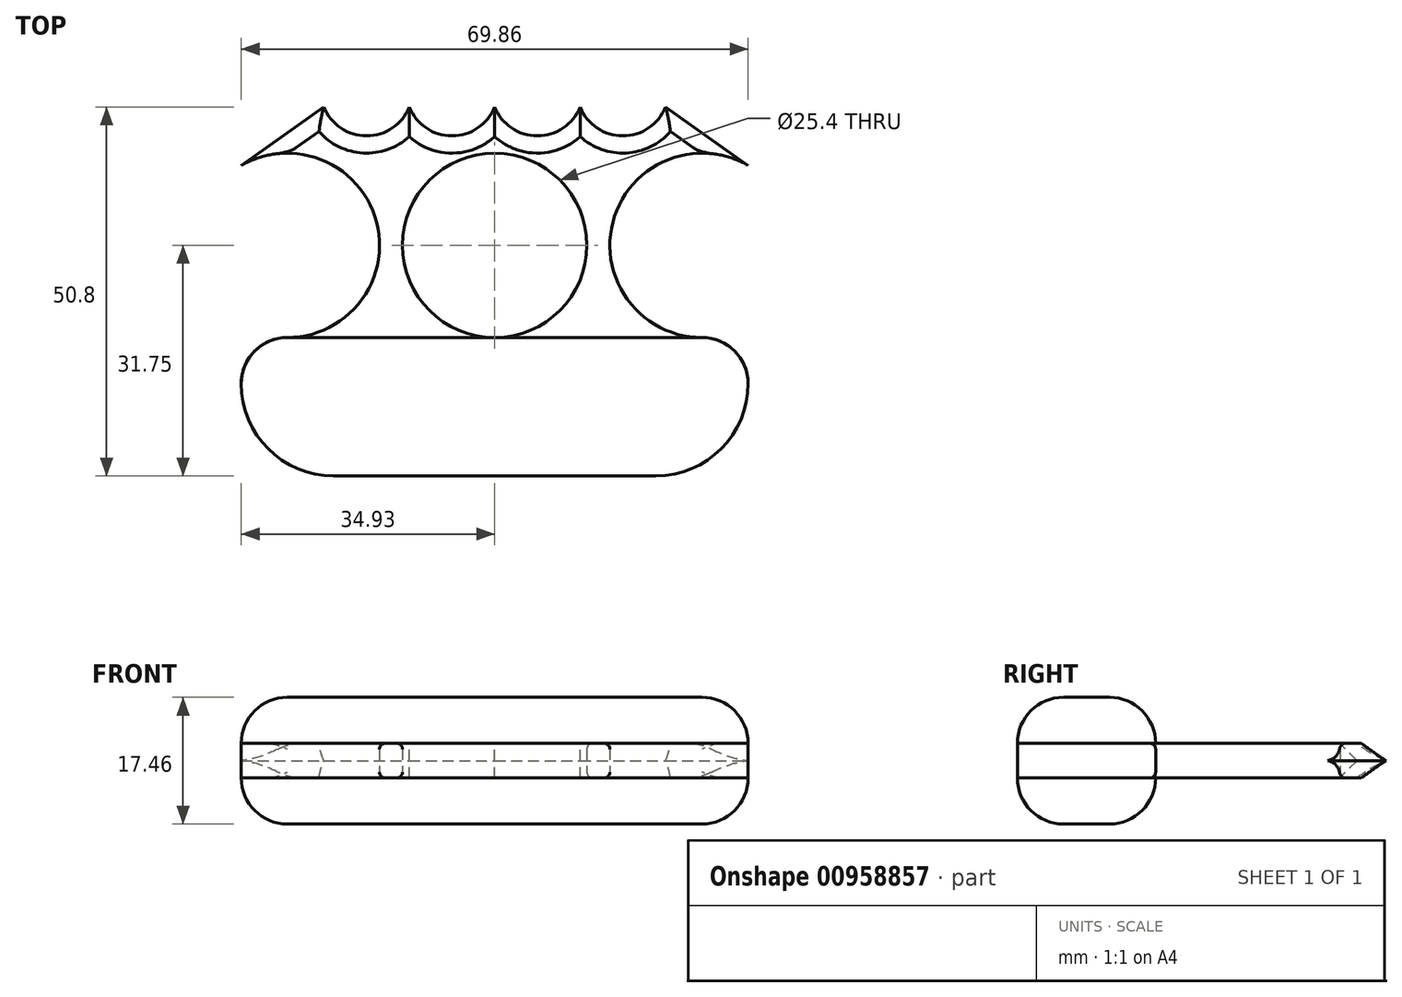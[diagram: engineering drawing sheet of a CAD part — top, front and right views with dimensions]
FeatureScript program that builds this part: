
annotation { "Feature Type Name" : "Feature", "Feature Type Description" : "" }
export const myFeature = defineFeature(function(context is Context, id is Id, definition is map)
    precondition{}
    {
        {
            var Q0;
            Q0=qCreatedBy(makeId("Top.planeOp"),FACE);
            var sketch = newSketch(context, id + "F0", { "sketchPlane" : qUnion([Q0])});
            skLineSegment(sketch, "E0.bottom", {"start": v(34.92, -25.4) * mm, "end": v(-34.92, -25.4) * mm});
            skLineSegment(sketch, "E0.top", {"start": v(34.92, 25.4) * mm, "end": v(-34.93, 25.4) * mm, "construction": true});
            skLineSegment(sketch, "E0.left", {"start": v(34.93, -25.4) * mm, "end": v(34.93, 25.4) * mm, "construction": true});
            skLineSegment(sketch, "E0.right", {"start": v(-34.92, -25.4) * mm, "end": v(-34.92, 25.4) * mm, "construction": true});
            skPoint(sketch, "E0.middle", {"position": v(0, 0) * mm});
            skCircle(sketch, "E1", {"center": v(0, 6.35) * mm, "radius": 12.7 * mm});
            skLineSegment(sketch, "E2", {"start": v(0, -6.35) * mm, "end": v(-34.92, -6.35) * mm, "construction": true});
            skLineSegment(sketch, "E3", {"start": v(0, -6.35) * mm, "end": v(34.93, -6.35) * mm, "construction": true});
            skArc(sketch, "E4", {"start": v(28.57, -6.35) * mm, "mid": v(16.3, 9.64) * mm, "end": v(34.92, 17.35) * mm});
            skArc(sketch, "E5", {"start": v(-28.58, -6.35) * mm, "mid": v(-16.3, 9.64) * mm, "end": v(-34.93, 17.35) * mm});
            skArc(sketch, "E6", {"start": v(28.57, -6.35) * mm, "mid": v(33.07, -8.2) * mm, "end": v(34.93, -12.7) * mm});
            skArc(sketch, "E7", {"start": v(-28.58, -6.35) * mm, "mid": v(-33.07, -8.2) * mm, "end": v(-34.93, -12.7) * mm});
            skArc(sketch, "E8", {"start": v(-34.93, -12.7) * mm, "mid": v(-31.2, -21.68) * mm, "end": v(-22.23, -25.4) * mm});
            skArc(sketch, "E9", {"start": v(34.93, -12.7) * mm, "mid": v(31.2, -21.68) * mm, "end": v(22.22, -25.4) * mm});
            skArc(sketch, "E10", {"start": v(-11.77, 25.4) * mm, "mid": v(-5.89, 21.43) * mm, "end": v(0, 25.4) * mm});
            skArc(sketch, "E11", {"start": v(-23.55, 25.4) * mm, "mid": v(-17.66, 21.43) * mm, "end": v(-11.77, 25.4) * mm});
            skLineSegment(sketch, "E12", {"start": v(-23.55, 25.4) * mm, "end": v(-34.93, 17.35) * mm});
            skLineSegment(sketch, "E13", {"start": v(0, 25.4) * mm, "end": v(0, -25.4) * mm, "construction": true});
            skArc(sketch, "E14.MirrorCS", {"start": v(11.77, 25.4) * mm, "mid": v(5.89, 21.43) * mm, "end": v(0, 25.4) * mm});
            skArc(sketch, "E15.MirrorCS", {"start": v(23.55, 25.4) * mm, "mid": v(17.66, 21.43) * mm, "end": v(11.77, 25.4) * mm});
            skLineSegment(sketch, "E16.MirrorCS", {"start": v(23.55, 25.4) * mm, "end": v(34.93, 17.35) * mm});
            skSolve(sketch);
        }
        {
            var Q0;
            Q0=makeQuery(id+"F0.imprint","IMPRINT",FACE,{"disambiguationData":[TD([[makeQuery(id+"F0.imprint","IMPRINT",EDGE,{"derivedFrom":sQuery(id+"F0.wireOp",EDGE,"E1")}),-1.0]])]});
            extrude(context, id + "F1", {"entities" : qUnion([Q0]), "depth" : 4.76 * mm, "offsetDistance" : 25.4 * mm});
        }
        {
            var Q0;
            Q0=makeQuery(id+"F1.opExtrude","CAP_EDGE",EDGE,{"disambiguationData":[OSD([sQuery(id+"F0.wireOp",EDGE,"E15.MirrorCS")])],"isStart":false});
            var Q1;
            Q1=makeQuery(id+"F1.opExtrude","CAP_EDGE",EDGE,{"disambiguationData":[OSD([sQuery(id+"F0.wireOp",EDGE,"E14.MirrorCS")])],"isStart":false});
            var Q2;
            Q2=makeQuery(id+"F1.opExtrude","CAP_EDGE",EDGE,{"disambiguationData":[OSD([sQuery(id+"F0.wireOp",EDGE,"E10")])],"isStart":false});
            var Q3;
            Q3=makeQuery(id+"F1.opExtrude","CAP_EDGE",EDGE,{"disambiguationData":[OSD([sQuery(id+"F0.wireOp",EDGE,"E11")])],"isStart":false});
            var Q4;
            Q4=makeQuery(id+"F1.opExtrude","CAP_EDGE",EDGE,{"disambiguationData":[OSD([sQuery(id+"F0.wireOp",EDGE,"E15.MirrorCS")])],"isStart":true});
            var Q5;
            Q5=makeQuery(id+"F1.opExtrude","CAP_EDGE",EDGE,{"disambiguationData":[OSD([sQuery(id+"F0.wireOp",EDGE,"E14.MirrorCS")])],"isStart":true});
            var Q6;
            Q6=makeQuery(id+"F1.opExtrude","CAP_EDGE",EDGE,{"disambiguationData":[OSD([sQuery(id+"F0.wireOp",EDGE,"E10")])],"isStart":true});
            var Q7;
            Q7=makeQuery(id+"F1.opExtrude","CAP_EDGE",EDGE,{"disambiguationData":[OSD([sQuery(id+"F0.wireOp",EDGE,"E11")])],"isStart":true});
            var Q8;
            Q8=makeQuery(id+"F1.opExtrude","CAP_EDGE",EDGE,{"disambiguationData":[OSD([sQuery(id+"F0.wireOp",EDGE,"E16.MirrorCS")])],"isStart":false});
            var Q9;
            Q9=makeQuery(id+"F1.opExtrude","CAP_EDGE",EDGE,{"disambiguationData":[OSD([sQuery(id+"F0.wireOp",EDGE,"E16.MirrorCS")])],"isStart":true});
            var Q10;
            Q10=makeQuery(id+"F1.opExtrude","CAP_EDGE",EDGE,{"disambiguationData":[OSD([sQuery(id+"F0.wireOp",EDGE,"E12")])],"isStart":false});
            var Q11;
            Q11=makeQuery(id+"F1.opExtrude","CAP_EDGE",EDGE,{"disambiguationData":[OSD([sQuery(id+"F0.wireOp",EDGE,"E12")])],"isStart":true});
            chamfer(context, id + "F2", {"entities" : qUnion([Q0, Q1, Q2, Q3, Q4, Q5, Q6, Q7, Q8, Q9, Q10, Q11]), "width" : 2.38 * mm, "tangentPropagation" : true});
        }
        {
            var Q0;
            Q0=makeQuery(id+"F1.opExtrude","CAP_FACE",FACE,{"disambiguationData":[OSD([sQuery(id+"F0.wireOp",EDGE,"E0.bottom"),sQuery(id+"F0.wireOp",EDGE,"E1"),sQuery(id+"F0.wireOp",EDGE,"E4"),sQuery(id+"F0.wireOp",EDGE,"E5"),sQuery(id+"F0.wireOp",EDGE,"E6"),sQuery(id+"F0.wireOp",EDGE,"E7"),sQuery(id+"F0.wireOp",EDGE,"E8"),sQuery(id+"F0.wireOp",EDGE,"E9"),sQuery(id+"F0.wireOp",EDGE,"E10"),sQuery(id+"F0.wireOp",EDGE,"E11"),sQuery(id+"F0.wireOp",EDGE,"E12"),sQuery(id+"F0.wireOp",EDGE,"E14.MirrorCS"),sQuery(id+"F0.wireOp",EDGE,"E15.MirrorCS"),sQuery(id+"F0.wireOp",EDGE,"E16.MirrorCS")])],"isStart":false});
            var sketch = newSketch(context, id + "F3", { "sketchPlane" : qUnion([Q0])});
            skLineSegment(sketch, "E17", {"start": v(-28.58, -6.35) * mm, "end": v(28.57, -6.35) * mm});
            skSolve(sketch);
        }
        {
            var Q0;
            Q0=makeQuery(id+"F3.imprint","IMPRINT",FACE,{"disambiguationData":[TD([[makeQuery(id+"F3.imprint","IMPRINT",EDGE,{"derivedFrom":makeQuery(id+"F1.opExtrude","CAP_EDGE",EDGE,{"disambiguationData":[OSD([sQuery(id+"F0.wireOp",EDGE,"E0.bottom")])],"isStart":false})}),-1.0]])]});
            extrude(context, id + "F4", {"entities" : qUnion([Q0]), "depth" : 6.35 * mm, "offsetDistance" : 25.4 * mm});
        }
        {
            var Q0;
            Q0=makeQuery(id+"F1.opExtrude","CAP_FACE",FACE,{"disambiguationData":[OSD([sQuery(id+"F0.wireOp",EDGE,"E0.bottom"),sQuery(id+"F0.wireOp",EDGE,"E1"),sQuery(id+"F0.wireOp",EDGE,"E4"),sQuery(id+"F0.wireOp",EDGE,"E5"),sQuery(id+"F0.wireOp",EDGE,"E6"),sQuery(id+"F0.wireOp",EDGE,"E7"),sQuery(id+"F0.wireOp",EDGE,"E8"),sQuery(id+"F0.wireOp",EDGE,"E9"),sQuery(id+"F0.wireOp",EDGE,"E10"),sQuery(id+"F0.wireOp",EDGE,"E11"),sQuery(id+"F0.wireOp",EDGE,"E12"),sQuery(id+"F0.wireOp",EDGE,"E14.MirrorCS"),sQuery(id+"F0.wireOp",EDGE,"E15.MirrorCS"),sQuery(id+"F0.wireOp",EDGE,"E16.MirrorCS")])],"isStart":true});
            var sketch = newSketch(context, id + "F5", { "sketchPlane" : qUnion([Q0])});
            skLineSegment(sketch, "E18", {"start": v(-28.58, 6.35) * mm, "end": v(28.57, 6.35) * mm});
            skSolve(sketch);
        }
        {
            var Q0;
            Q0=makeQuery(id+"F5.imprint","IMPRINT",FACE,{"disambiguationData":[TD([[makeQuery(id+"F5.imprint","IMPRINT",EDGE,{"derivedFrom":makeQuery(id+"F1.opExtrude","CAP_EDGE",EDGE,{"disambiguationData":[OSD([sQuery(id+"F0.wireOp",EDGE,"E0.bottom")])],"isStart":true})}),1.0]])]});
            extrude(context, id + "F6", {"entities" : qUnion([Q0]), "depth" : 6.35 * mm, "offsetDistance" : 25.4 * mm});
        }
        {
            var Q0;
            Q0=makeQuery(id+"F4.opExtrude","CAP_FACE",FACE,{"disambiguationData":[OSD([sQuery(id+"F0.wireOp",EDGE,"E0.bottom"),sQuery(id+"F0.wireOp",EDGE,"E6"),sQuery(id+"F0.wireOp",EDGE,"E7"),sQuery(id+"F0.wireOp",EDGE,"E8"),sQuery(id+"F0.wireOp",EDGE,"E9"),sQuery(id+"F3.wireOp",EDGE,"E17")])],"isStart":false});
            var Q1;
            Q1=makeQuery(id+"F6.opExtrude","CAP_FACE",FACE,{"disambiguationData":[OSD([sQuery(id+"F0.wireOp",EDGE,"E0.bottom"),sQuery(id+"F0.wireOp",EDGE,"E6"),sQuery(id+"F0.wireOp",EDGE,"E7"),sQuery(id+"F0.wireOp",EDGE,"E8"),sQuery(id+"F0.wireOp",EDGE,"E9"),sQuery(id+"F5.wireOp",EDGE,"E18")])],"isStart":false});
            fillet(context, id + "F7", {"entities" : qUnion([Q0, Q1]), "radius" : 6.35 * mm, "tangentPropagation" : true, "allowEdgeOverflow" : false});
        }
        {
            var Q0;
            Q0=makeQuery(id+"F1.opExtrude","CAP_EDGE",EDGE,{"disambiguationData":[OSD([sQuery(id+"F0.wireOp",EDGE,"E4")])],"isStart":true});
            var Q1;
            Q1=makeQuery(id+"F1.opExtrude","CAP_EDGE",EDGE,{"disambiguationData":[OSD([sQuery(id+"F0.wireOp",EDGE,"E1")])],"isStart":true});
            var Q2;
            Q2=makeQuery(id+"F1.opExtrude","CAP_EDGE",EDGE,{"disambiguationData":[OSD([sQuery(id+"F0.wireOp",EDGE,"E1")])],"isStart":false});
            var Q3;
            Q3=makeQuery(id+"F1.opExtrude","CAP_EDGE",EDGE,{"disambiguationData":[OSD([sQuery(id+"F0.wireOp",EDGE,"E5")])],"isStart":true});
            var Q4;
            Q4=makeQuery(id+"F1.opExtrude","CAP_EDGE",EDGE,{"disambiguationData":[OSD([sQuery(id+"F0.wireOp",EDGE,"E4")])],"isStart":false});
            var Q5;
            Q5=makeQuery(id+"F1.opExtrude","CAP_EDGE",EDGE,{"disambiguationData":[OSD([sQuery(id+"F0.wireOp",EDGE,"E5")])],"isStart":false});
            fillet(context, id + "F8", {"entities" : qUnion([Q0, Q1, Q2, Q3, Q4, Q5]), "radius" : 0.8 * mm, "allowEdgeOverflow" : false});
        }
    });
